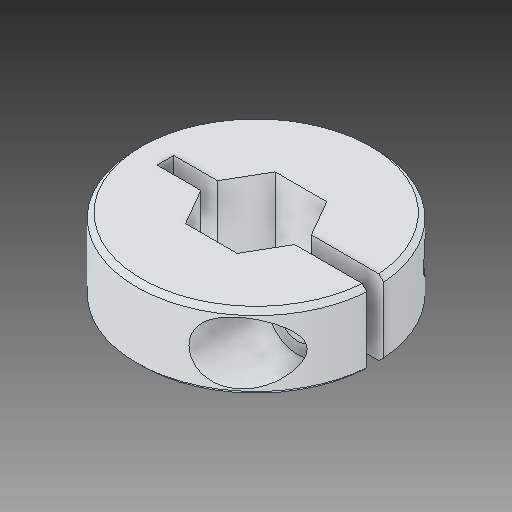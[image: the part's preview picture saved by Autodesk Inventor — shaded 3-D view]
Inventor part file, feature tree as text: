
AUTODESK INVENTOR PART (.ipt)
format: ipt  version: 2018 (Build 220112000, 112)  size: 141,824 bytes
history: native  units: in
note: dims shown in document units (in); Inventor stores cm internally (conversion verified against a paired STEP export)
features: chamfer x1
ambient origin geometry x8: Origin, YZ Plane, XZ Plane, XY Plane, X Axis, Y Axis, Z Axis, Center Point
bodies: Solid1 (feature_tree)
feature tree (1):
  chamfer  "Chamfer1"  [1 undecoded]
note: 1 required parameter value undecoded (feature->parameter linkage not recoverable at this tier; creation-order binding heuristic only, values carry confidence <= 0.55)
